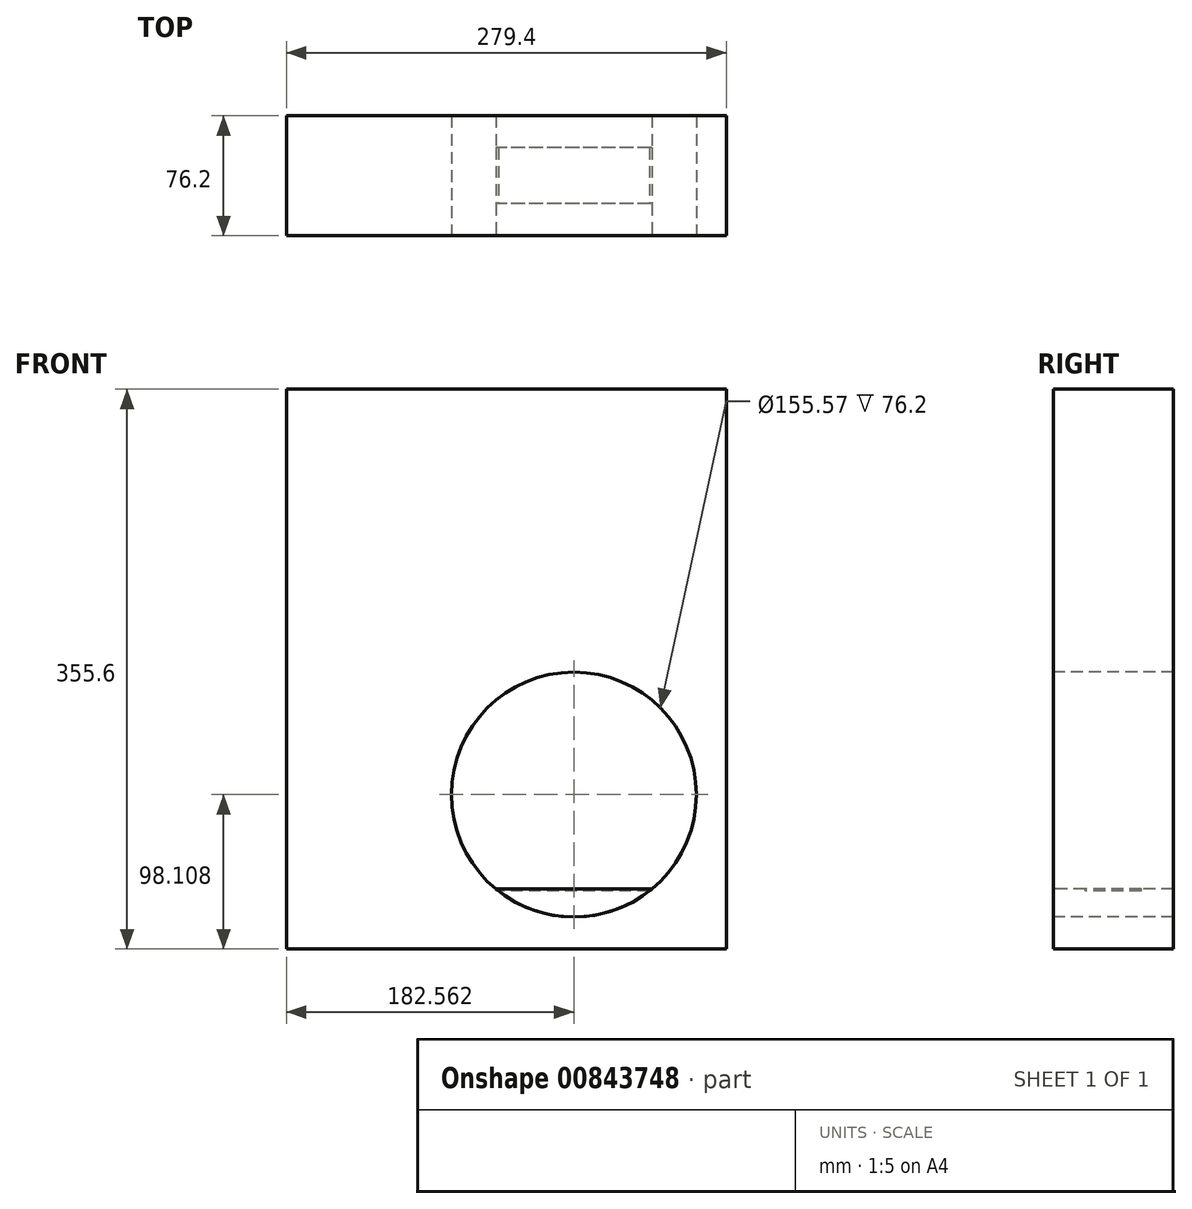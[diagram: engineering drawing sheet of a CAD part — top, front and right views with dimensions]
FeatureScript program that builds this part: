
annotation { "Feature Type Name" : "Feature", "Feature Type Description" : "" }
export const myFeature = defineFeature(function(context is Context, id is Id, definition is map)
    precondition{}
    {
        {
            var Q0;
            Q0=qCreatedBy(makeId("Front.planeOp"),FACE);
            var sketch = newSketch(context, id + "F0", { "sketchPlane" : qUnion([Q0])});
            skLineSegment(sketch, "E0.bottom", {"start": v(0, 0) * mm, "end": v(279.4, 0) * mm});
            skLineSegment(sketch, "E0.top", {"start": v(0, 355.6) * mm, "end": v(279.4, 355.6) * mm});
            skLineSegment(sketch, "E0.left", {"start": v(0, 0) * mm, "end": v(0, 355.6) * mm});
            skLineSegment(sketch, "E0.right", {"start": v(279.4, 0) * mm, "end": v(279.4, 355.6) * mm});
            skSolve(sketch);
        }
        {
            var Q0;
            Q0 = qSketchRegion(id + "F0", true);
            extrude(context, id + "F1", {"entities" : qUnion([Q0]), "endBound" : BoundingType.SYMMETRIC, "depth" : 76.2 * mm, "offsetDistance" : 25.4 * mm});
        }
        {
            var Q0;
            Q0=makeQuery(id+"F1.opExtrude","CAP_FACE",FACE,{"disambiguationData":[OSD([sQuery(id+"F0.wireOp",EDGE,"E0.bottom"),sQuery(id+"F0.wireOp",EDGE,"E0.top"),sQuery(id+"F0.wireOp",EDGE,"E0.left"),sQuery(id+"F0.wireOp",EDGE,"E0.right")])],"isStart":false});
            var sketch = newSketch(context, id + "F2", { "sketchPlane" : qUnion([Q0])});
            skCircle(sketch, "E1", {"center": v(182.56, 98.1) * mm, "radius": 77.79 * mm});
            skSolve(sketch);
        }
        {
            var Q0;
            Q0 = qSketchRegion(id + "F2", true);
            extrude(context, id + "F3", {"entities" : qUnion([Q0]), "operationType" : NewBodyOperationType.REMOVE, "endBound" : BoundingType.THROUGH_ALL, "oppositeDirection" : true, "depth" : 25.4 * mm, "offsetDistance" : 25.4 * mm});
        }
        {
            var Q0;
            Q0=makeQuery(id+"F1.opExtrude","CAP_FACE",FACE,{"disambiguationData":[OSD([sQuery(id+"F0.wireOp",EDGE,"E0.bottom"),sQuery(id+"F0.wireOp",EDGE,"E0.top"),sQuery(id+"F0.wireOp",EDGE,"E0.left"),sQuery(id+"F0.wireOp",EDGE,"E0.right")])],"isStart":false});
            var sketch = newSketch(context, id + "F4", { "sketchPlane" : qUnion([Q0])});
            skArc(sketch, "E2", {"start": v(133.07, 38.1) * mm, "mid": v(182.56, 20.32) * mm, "end": v(232.06, 38.1) * mm});
            skLineSegment(sketch, "E3", {"start": v(182.56, 20.32) * mm, "end": v(182.56, 38.1) * mm, "construction": true});
            skLineSegment(sketch, "E4", {"start": v(182.56, 38.1) * mm, "end": v(232.06, 38.1) * mm});
            skLineSegment(sketch, "E5", {"start": v(182.56, 38.1) * mm, "end": v(133.07, 38.1) * mm});
            skSolve(sketch);
        }
        {
            var Q0;
            Q0 = qSketchRegion(id + "F4", true);
            var Q1;
            Q1=makeQuery(id+"F1.opExtrude","CAP_FACE",FACE,{"disambiguationData":[OSD([sQuery(id+"F0.wireOp",EDGE,"E0.bottom"),sQuery(id+"F0.wireOp",EDGE,"E0.top"),sQuery(id+"F0.wireOp",EDGE,"E0.left"),sQuery(id+"F0.wireOp",EDGE,"E0.right")])],"isStart":true});
            extrude(context, id + "F5", {"entities" : qUnion([Q0]), "endBound" : BoundingType.UP_TO_SURFACE, "oppositeDirection" : true, "depth" : 25.4 * mm, "endBoundEntityFace" : qUnion([Q1]), "offsetDistance" : 25.4 * mm});
        }
        {
            var Q0;
            Q0=makeQuery(id+"F5.opExtrude","SWEPT_FACE",FACE,{"disambiguationData":[OSD([sQuery(id+"F4.wireOp",EDGE,"E4"),sQuery(id+"F4.wireOp",EDGE,"E5")])]});
            var sketch = newSketch(context, id + "F6", { "sketchPlane" : qUnion([Q0])});
            skLineSegment(sketch, "E6", {"start": v(133.07, 0) * mm, "end": v(232.06, 0) * mm, "construction": true});
            skLineSegment(sketch, "E7", {"start": v(182.56, 38.1) * mm, "end": v(182.56, -38.1) * mm, "construction": true});
            skLineSegment(sketch, "E8.bottom", {"start": v(232.1, -17.78) * mm, "end": v(133.03, -17.78) * mm});
            skLineSegment(sketch, "E8.top", {"start": v(232.1, 17.78) * mm, "end": v(133.03, 17.78) * mm});
            skLineSegment(sketch, "E8.left", {"start": v(232.1, -17.78) * mm, "end": v(232.1, 17.78) * mm});
            skLineSegment(sketch, "E8.right", {"start": v(133.03, -17.78) * mm, "end": v(133.03, 17.78) * mm});
            skPoint(sketch, "E8.middle", {"position": v(182.56, 0) * mm});
            skSolve(sketch);
        }
        {
            var Q0;
            {var subQ0=sQuery(id+"F6.wireOp",EDGE,"E8.bottom");var subQ1=sQuery(id+"F4.wireOp",EDGE,"E2");var subQ2=sQuery(id+"F2.wireOp",EDGE,"E1");var subQ3=makeQuery(id+"F5.opExtrude","SWEPT_EDGE",EDGE,{"disambiguationData":[OSD([subQ2,subQ1,sQuery(id+"F4.wireOp",EDGE,"E4")])]});var subQ4=makeQuery(id+"F6.imprint","INTERSECT",VERTEX,{"derivedFrom":[subQ3,subQ0]});Q0=makeQuery(id+"F6.imprint","IMPRINT",FACE,{"disambiguationData":[TD([[makeQuery(id+"F6.imprint","IMPRINT",EDGE,{"disambiguationData":[TD([[subQ4,-1.0]])],"derivedFrom":subQ0}),-1.0]])]});}
            extrude(context, id + "F7", {"entities" : qUnion([Q0]), "operationType" : NewBodyOperationType.REMOVE, "oppositeDirection" : true, "depth" : 1.27 * mm, "offsetDistance" : 25.4 * mm});
        }
    });
